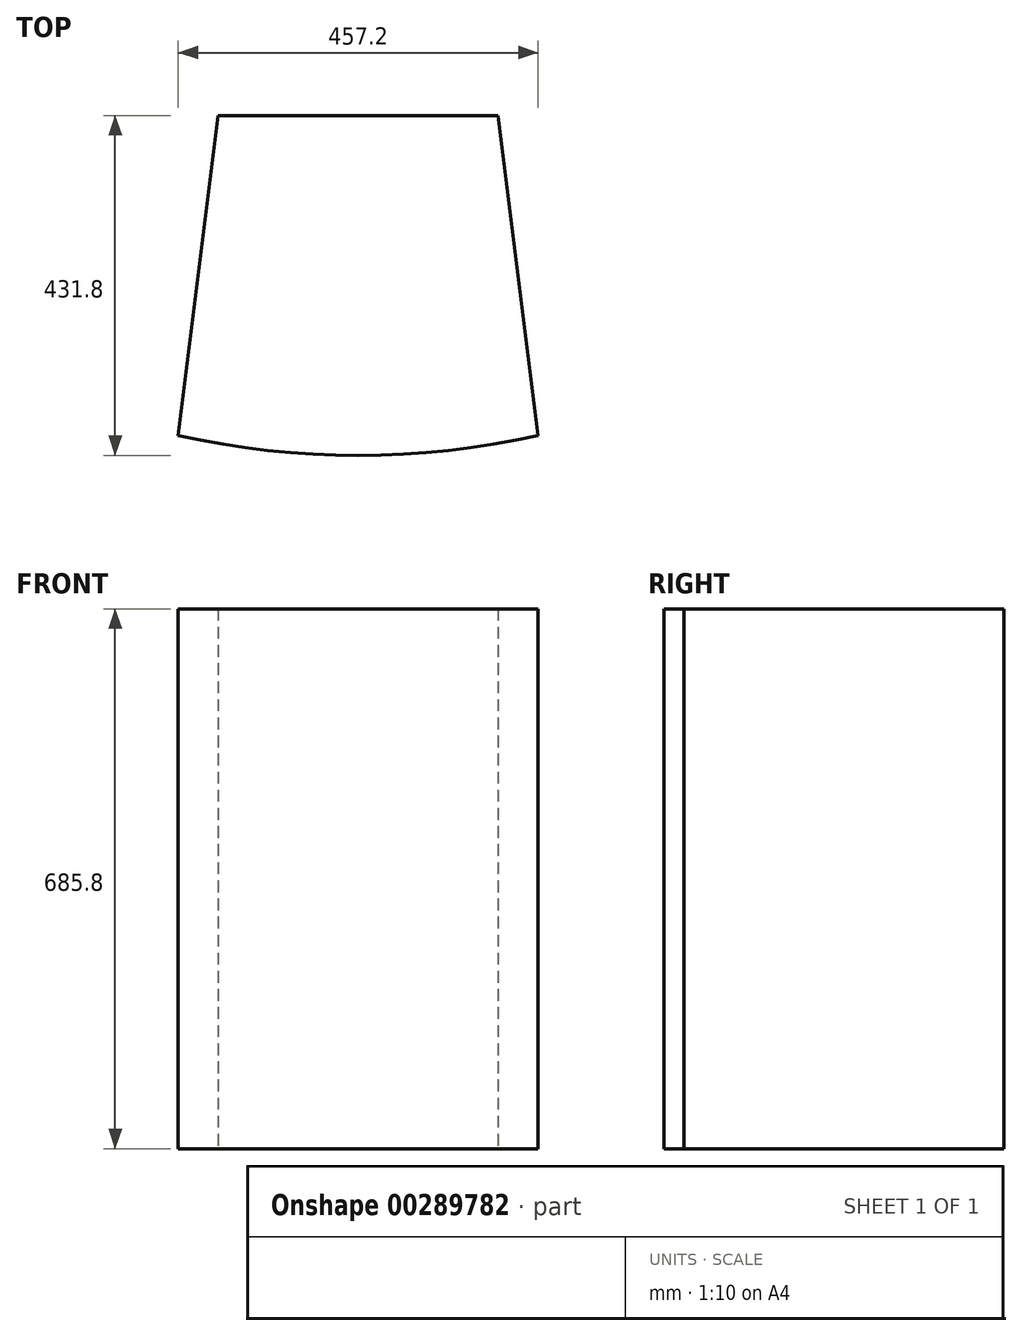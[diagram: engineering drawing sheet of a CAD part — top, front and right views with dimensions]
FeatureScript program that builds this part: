
annotation { "Feature Type Name" : "Feature", "Feature Type Description" : "" }
export const myFeature = defineFeature(function(context is Context, id is Id, definition is map)
    precondition{}
    {
        {
            var Q0;
            Q0=qCreatedBy(makeId("Top.planeOp"),FACE);
            var sketch = newSketch(context, id + "F0", { "sketchPlane" : qUnion([Q0])});
            skLineSegment(sketch, "E0", {"start": v(-177.8, 0) * mm, "end": v(177.8, 0) * mm});
            skLineSegment(sketch, "E1", {"start": v(-177.8, 0) * mm, "end": v(-228.6, -406.4) * mm});
            skLineSegment(sketch, "E2", {"start": v(0, 0) * mm, "end": v(0, -431.8) * mm, "construction": true});
            skLineSegment(sketch, "E3", {"start": v(228.6, -406.4) * mm, "end": v(177.8, 0) * mm});
            skArc(sketch, "E4", {"start": v(-228.6, -406.4) * mm, "mid": v(0, -431.8) * mm, "end": v(228.6, -406.4) * mm});
            skLineSegment(sketch, "E5", {"start": v(-228.6, -406.4) * mm, "end": v(228.6, -406.4) * mm, "construction": true});
            skSolve(sketch);
        }
        {
            var Q0;
            Q0=makeQuery(id+"F0.imprint","IMPRINT",FACE,{"disambiguationData":[TD([[makeQuery(id+"F0.imprint","IMPRINT",EDGE,{"derivedFrom":sQuery(id+"F0.wireOp",EDGE,"E0")}),-1.0]])]});
            extrude(context, id + "F1", {"entities" : qUnion([Q0]), "depth" : 685.8 * mm});
        }
    });
